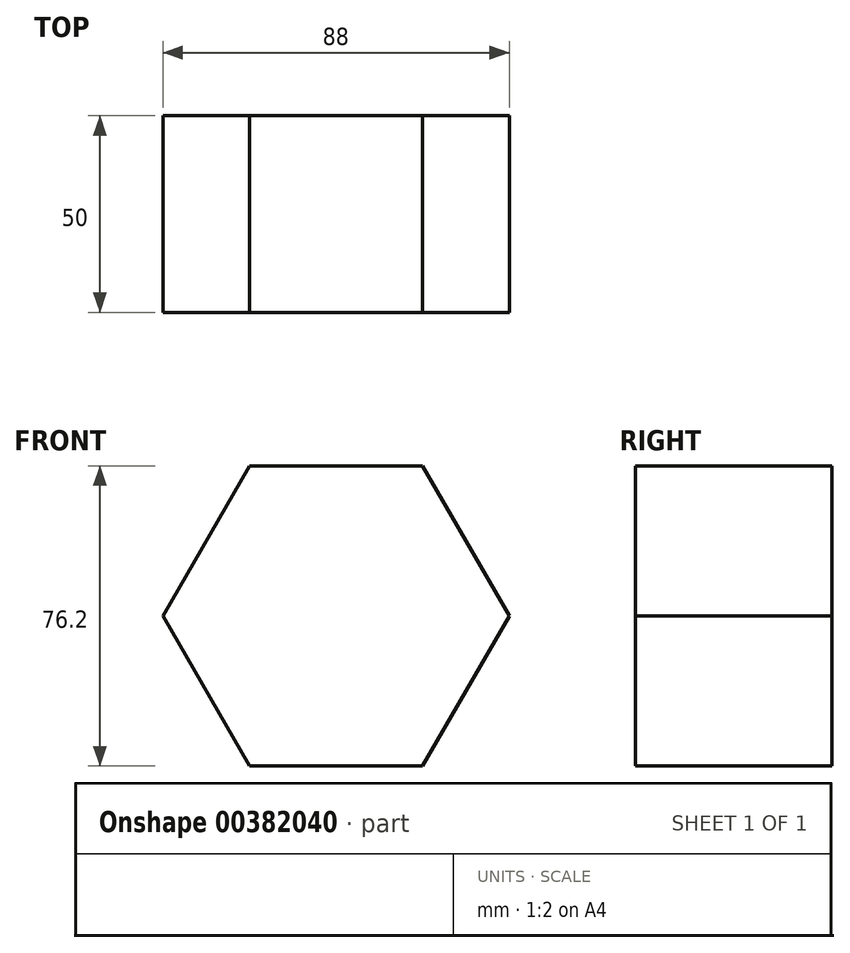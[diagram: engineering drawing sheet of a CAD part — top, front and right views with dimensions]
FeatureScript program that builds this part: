
annotation { "Feature Type Name" : "Feature", "Feature Type Description" : "" }
export const myFeature = defineFeature(function(context is Context, id is Id, definition is map)
    precondition{}
    {
        {
            var Q0;
            Q0=qCreatedBy(makeId("Front.planeOp"),FACE);
            var sketch = newSketch(context, id + "F0", { "sketchPlane" : qUnion([Q0])});
            skCircle(sketch, "E0.cCircle", {"center": v(0, 0) * mm, "radius": 38.1 * mm, "construction": true});
            skLineSegment(sketch, "E0.0", {"start": v(-22, 38.1) * mm, "end": v(22, 38.1) * mm});
            skLineSegment(sketch, "E0.1", {"start": v(22, 38.1) * mm, "end": v(44, 0) * mm});
            skLineSegment(sketch, "E0.2", {"start": v(44, 0) * mm, "end": v(22, -38.1) * mm});
            skLineSegment(sketch, "E0.3", {"start": v(22, -38.1) * mm, "end": v(-22, -38.1) * mm});
            skLineSegment(sketch, "E0.4", {"start": v(-22, -38.1) * mm, "end": v(-44, 0) * mm});
            skLineSegment(sketch, "E0.5", {"start": v(-44, 0) * mm, "end": v(-22, 38.1) * mm});
            skPoint(sketch, "E0.0.midPoint", {"position": v(0, 38.1) * mm});
            skSolve(sketch);
        }
        {
            var Q0;
            Q0 = qSketchRegion(id + "F0", true);
            extrude(context, id + "F1", {"entities" : qUnion([Q0]), "depth" : 50 * mm});
        }
    });
